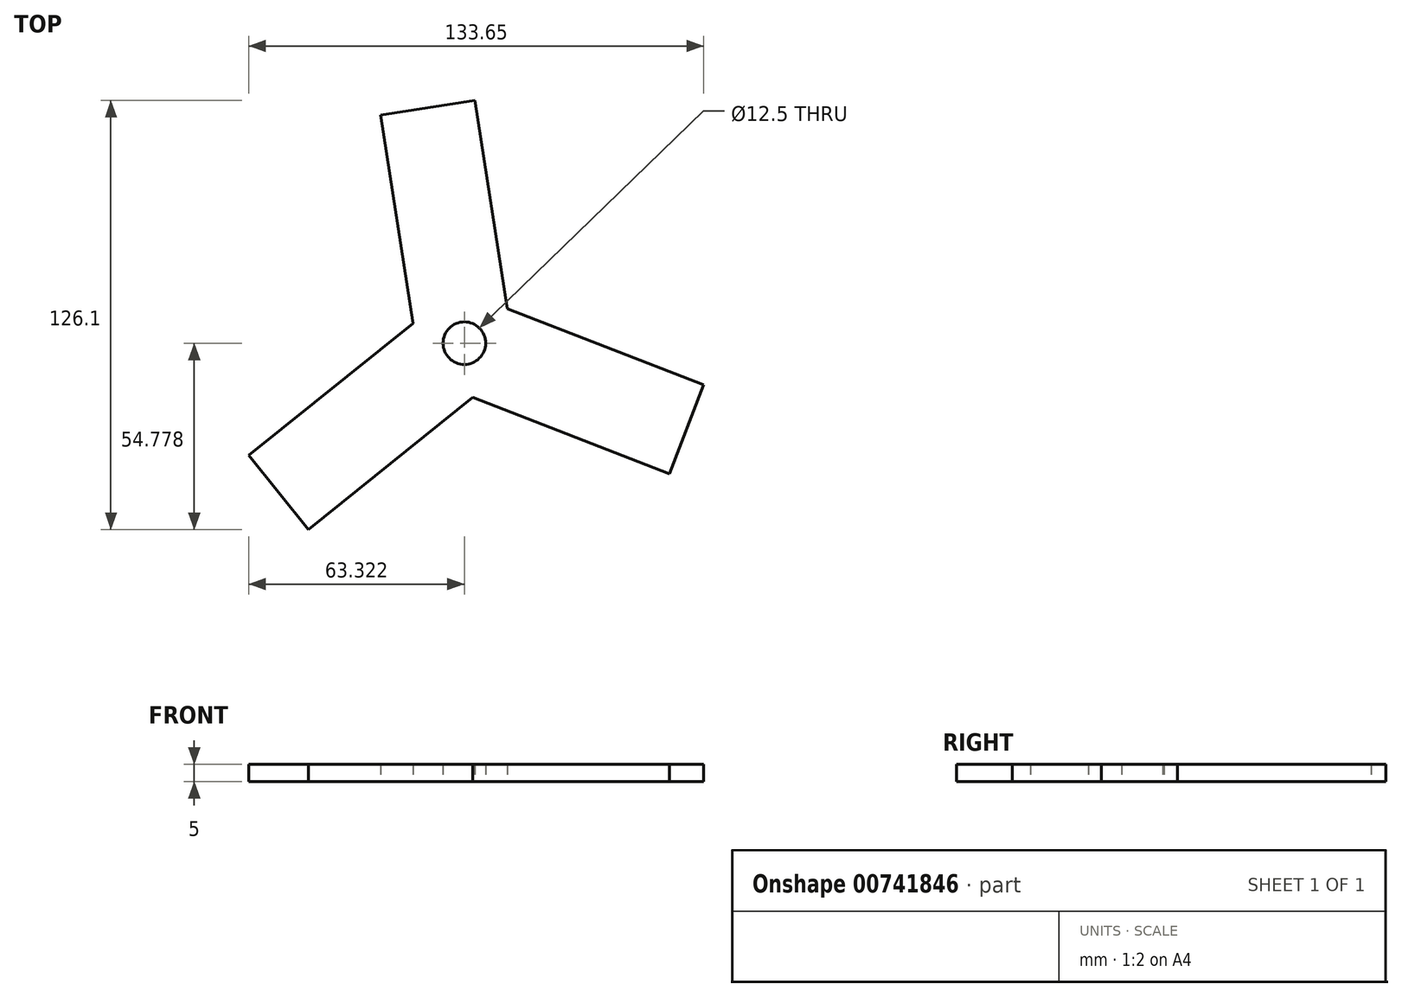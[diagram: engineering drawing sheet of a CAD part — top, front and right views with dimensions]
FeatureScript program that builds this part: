
annotation { "Feature Type Name" : "Feature", "Feature Type Description" : "" }
export const myFeature = defineFeature(function(context is Context, id is Id, definition is map)
    precondition{}
    {
        {
            var Q0;
            Q0=qCreatedBy(makeId("Top.planeOp"),FACE);
            var sketch = newSketch(context, id + "F0", { "sketchPlane" : qUnion([Q0])});
            skLineSegment(sketch, "E0.bottom", {"start": v(-32.04, 75.34) * mm, "end": v(-4.37, 79.63) * mm});
            skLineSegment(sketch, "E0.left", {"start": v(-32.04, 75.34) * mm, "end": v(-22.55, 14.15) * mm});
            skLineSegment(sketch, "E0.right", {"start": v(-4.37, 79.63) * mm, "end": v(5.12, 18.44) * mm});
            skLineSegment(sketch, "E1", {"start": v(-22.55, 14.15) * mm, "end": v(-70.8, -24.66) * mm});
            skLineSegment(sketch, "E2", {"start": v(-70.8, -24.66) * mm, "end": v(-53.25, -46.47) * mm});
            skLineSegment(sketch, "E3", {"start": v(-53.25, -46.47) * mm, "end": v(-5, -7.67) * mm});
            skLineSegment(sketch, "E4", {"start": v(-5, -7.67) * mm, "end": v(52.73, -30.05) * mm});
            skLineSegment(sketch, "E5", {"start": v(52.73, -30.05) * mm, "end": v(62.85, -3.94) * mm});
            skLineSegment(sketch, "E6", {"start": v(62.85, -3.94) * mm, "end": v(5.12, 18.44) * mm});
            skLineSegment(sketch, "E7", {"start": v(-22.55, 14.15) * mm, "end": v(17.33, -1.3) * mm});
            skLineSegment(sketch, "E8", {"start": v(-5, -7.67) * mm, "end": v(-9.45, 21.02) * mm});
            skCircle(sketch, "E9", {"center": v(-7.48, 8.3) * mm, "radius": 6.25 * mm});
            skSolve(sketch);
        }
        {
            var Q0;
            Q0 = qSketchRegion(id + "F0", true);
            extrude(context, id + "F1", {"entities" : qUnion([Q0]), "depth" : 5 * mm, "offsetDistance" : 25 * mm});
        }
    });
